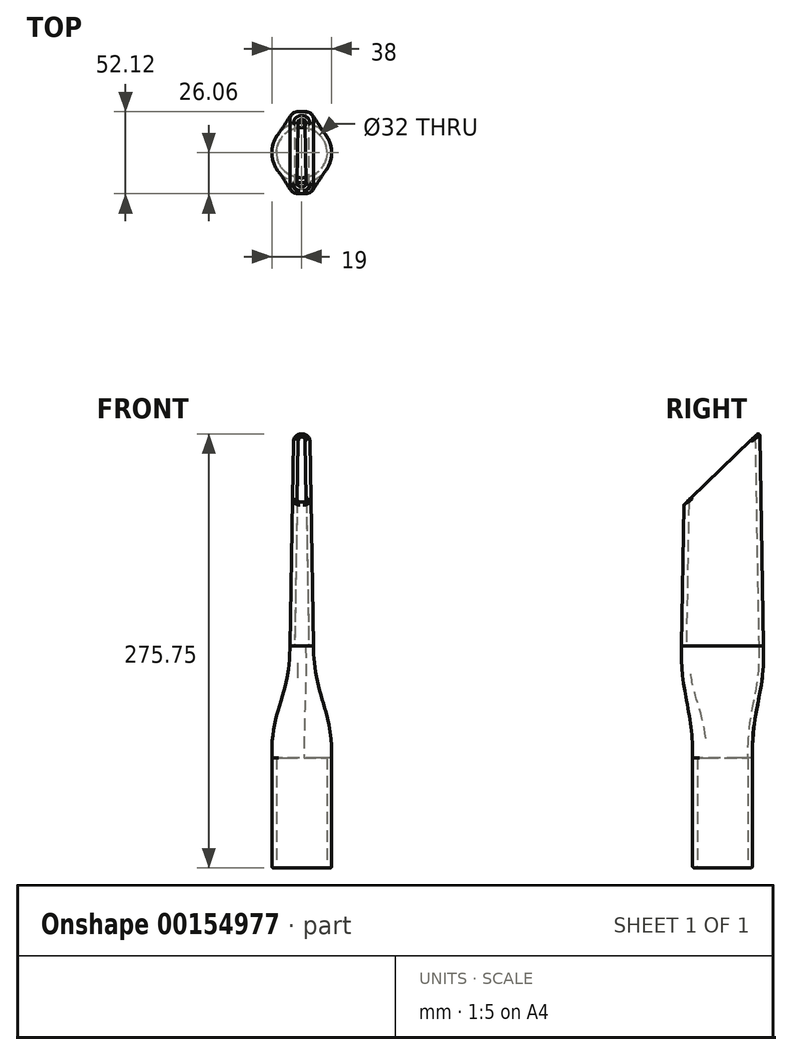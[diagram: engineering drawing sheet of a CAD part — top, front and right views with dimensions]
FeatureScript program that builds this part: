
annotation { "Feature Type Name" : "Feature", "Feature Type Description" : "" }
export const myFeature = defineFeature(function(context is Context, id is Id, definition is map)
    precondition{}
    {
        {
            var Q0;
            Q0=qCreatedBy(makeId("Top.planeOp"),FACE);
            var sketch = newSketch(context, id + "F0", { "sketchPlane" : qUnion([Q0])});
            skCircle(sketch, "E0", {"center": v(0, 0) * mm, "radius": 19 * mm});
            skSolve(sketch);
        }
        {
            var Q0;
            Q0=makeQuery(id+"F0.imprint","IMPRINT",FACE,{"disambiguationData":[TD([[makeQuery(id+"F0.imprint","IMPRINT",EDGE,{"derivedFrom":sQuery(id+"F0.wireOp",EDGE,"E0")}),1.0]])]});
            extrude(context, id + "F1", {"entities" : qUnion([Q0]), "depth" : 70 * mm});
        }
        {
            var Q0;
            Q0=qCreatedBy(makeId("Top.planeOp"),FACE);
            cPlane(context, id + "F2", {"entities" : qUnion([Q0]), "cplaneType" : CPlaneType.OFFSET, "offset" : 141 * mm, "width" : 150 * mm, "height" : 150 * mm});
        }
        {
            var Q0;
            Q0=qCreatedBy(id+"F2.planeOp",FACE);
            var sketch = newSketch(context, id + "F3", { "sketchPlane" : qUnion([Q0])});
            skLineSegment(sketch, "E1.bottom", {"start": v(7.5, 26) * mm, "end": v(-7.5, 26) * mm});
            skLineSegment(sketch, "E1.top", {"start": v(7.5, -26) * mm, "end": v(-7.5, -26) * mm});
            skLineSegment(sketch, "E1.left", {"start": v(7.5, 26) * mm, "end": v(7.5, -26) * mm});
            skLineSegment(sketch, "E1.right", {"start": v(-7.5, 26) * mm, "end": v(-7.5, -26) * mm});
            skPoint(sketch, "E1.middle", {"position": v(0, 0) * mm});
            skSolve(sketch);
        }
        {
            var Q0;
            Q0=makeQuery(id+"F3.imprint","IMPRINT",FACE,{"disambiguationData":[TD([[makeQuery(id+"F3.imprint","IMPRINT",EDGE,{"derivedFrom":sQuery(id+"F3.wireOp",EDGE,"E1.bottom")}),1.0]])]});
            extrude(context, id + "F4", {"entities" : qUnion([Q0]), "depth" : 136 * mm, "hasDraft" : true, "draftAngle" : 1 * degree, "draftPullDirection" : true});
        }
        {
            var Q0;
            Q0=makeQuery(id+"F4.opExtrude","SWEPT_EDGE",EDGE,{"disambiguationData":[OSD([sQuery(id+"F3.wireOp",EDGE,"E1.top"),sQuery(id+"F3.wireOp",EDGE,"E1.left")])]});
            var Q1;
            Q1=makeQuery(id+"F4.opExtrude","SWEPT_EDGE",EDGE,{"disambiguationData":[OSD([sQuery(id+"F3.wireOp",EDGE,"E1.top"),sQuery(id+"F3.wireOp",EDGE,"E1.right")])]});
            var Q2;
            Q2=makeQuery(id+"F4.opExtrude","SWEPT_EDGE",EDGE,{"disambiguationData":[OSD([sQuery(id+"F3.wireOp",EDGE,"E1.bottom"),sQuery(id+"F3.wireOp",EDGE,"E1.left")])]});
            var Q3;
            Q3=makeQuery(id+"F4.opExtrude","SWEPT_EDGE",EDGE,{"disambiguationData":[OSD([sQuery(id+"F3.wireOp",EDGE,"E1.bottom"),sQuery(id+"F3.wireOp",EDGE,"E1.right")])]});
            fillet(context, id + "F5", {"entities" : qUnion([Q0, Q1, Q2, Q3]), "radius" : 5 * mm, "tangentPropagation" : true, "allowEdgeOverflow" : false});
        }
        {
            var Q0;
            Q0=makeQuery(id+"F4.opExtrude","CAP_FACE",FACE,{"disambiguationData":[OSD([sQuery(id+"F3.wireOp",EDGE,"E1.bottom"),sQuery(id+"F3.wireOp",EDGE,"E1.top"),sQuery(id+"F3.wireOp",EDGE,"E1.left"),sQuery(id+"F3.wireOp",EDGE,"E1.right")])],"isStart":true});
            var Q1;
            Q1=makeQuery(id+"F1.opExtrude","CAP_FACE",FACE,{"disambiguationData":[OSD([sQuery(id+"F0.wireOp",EDGE,"E0")])],"isStart":false});
            loft(context, id + "F6", {"operationType" : NewBodyOperationType.ADD, "startCondition" : LoftEndDerivativeType.MATCH_CURVATURE, "startMagnitude" : 1, "endCondition" : LoftEndDerivativeType.MATCH_CURVATURE, "endMagnitude" : 1, "sheetProfilesArray" : [{ "sheetProfileEntities" : qUnion([Q0]) }, { "sheetProfileEntities" : qUnion([Q1]) }]});
        }
        {
            var Q0;
            Q0=qCreatedBy(makeId("Right.planeOp"),FACE);
            var sketch = newSketch(context, id + "F7", { "sketchPlane" : qUnion([Q0])});
            skPoint(sketch, "E2.0", {"position": v(23.67, 277.1) * mm});
            skPoint(sketch, "E3.0", {"position": v(-26, 141) * mm});
            skLineSegment(sketch, "E4", {"start": v(-26, 229.34) * mm, "end": v(23.67, 277.1) * mm});
            skLineSegment(sketch, "E5", {"start": v(23.67, 277.1) * mm, "end": v(-24.87, 307.3) * mm});
            skLineSegment(sketch, "E6", {"start": v(-24.87, 307.3) * mm, "end": v(-54.4, 295.59) * mm});
            skLineSegment(sketch, "E7", {"start": v(-54.4, 295.59) * mm, "end": v(-43.3, 241.47) * mm});
            skLineSegment(sketch, "E8", {"start": v(-43.3, 241.47) * mm, "end": v(-26, 229.34) * mm});
            skPoint(sketch, "E9.0", {"position": v(23.63, 277) * mm});
            skSolve(sketch);
        }
        {
            var Q0;
            Q0=makeQuery(id+"F7.imprint","IMPRINT",FACE,{"disambiguationData":[TD([[makeQuery(id+"F7.imprint","IMPRINT",EDGE,{"derivedFrom":sQuery(id+"F7.wireOp",EDGE,"E4")}),1.0]])]});
            extrude(context, id + "F8", {"entities" : qUnion([Q0]), "operationType" : NewBodyOperationType.REMOVE, "endBound" : BoundingType.SYMMETRIC, "depth" : 149.5 * mm});
        }
        {
            var Q0;
            Q0=makeQuery(id+"F8.boolean.opBoolean","COPY",FACE,{"derivedFrom":makeQuery(id+"F8.opExtrude","SWEPT_FACE",FACE,{"disambiguationData":[OSD([sQuery(id+"F7.wireOp",EDGE,"E4")])]})});
            var Q1;
            Q1=makeQuery(id+"F1.opExtrude","CAP_FACE",FACE,{"disambiguationData":[OSD([sQuery(id+"F0.wireOp",EDGE,"E0")])],"isStart":true});
            shell(context, id + "F9", {"entities" : qUnion([Q0, Q1]), "thickness" : 3 * mm});
        }
        {
            var Q0;
            Q0=makeQuery(id+"F8.boolean.opBoolean","COPY",FACE,{"derivedFrom":makeQuery(id+"F8.opExtrude","SWEPT_FACE",FACE,{"disambiguationData":[OSD([sQuery(id+"F7.wireOp",EDGE,"E4")])]})});
            var Q1;
            Q1=makeQuery(id+"F1.opExtrude","CAP_FACE",FACE,{"disambiguationData":[OSD([sQuery(id+"F0.wireOp",EDGE,"E0")])],"isStart":true});
            fillet(context, id + "F10", {"entities" : qUnion([Q0, Q1]), "radius" : 1 * mm, "tangentPropagation" : true, "allowEdgeOverflow" : false});
        }
    });
